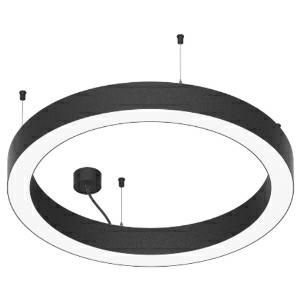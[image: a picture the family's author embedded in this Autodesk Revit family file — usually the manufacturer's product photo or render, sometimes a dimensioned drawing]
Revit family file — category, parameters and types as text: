
# Revit family: glorious_slim_410-9634
name_source: partatom
category: Leuchten
revit_build: Autodesk Revit 2016 (Build: 20190508_0715(x64)
units: mm (PartAtom-declared; Revit-internal decimal feet)

## family parameters
Basisbauteil = Fläche
Beim Laden mit Abzugskörper schneiden = Nein
Bemaßung runder Anschluss = Durchmesser verwenden
Gemeinsam genutzt = Nein
Lichtquelle = Nein
Raumberechnungspunkt = Nein
Teiletyp = Normal

## types (1)
- 410-9634-D01-H27 (1 x LED, 405.68 lm, 3.1 W, 2700K)
    Beschreibung = GLORIOUS SLIM
    CIE Flux Codes = 48 79 96 100 78
    Color Rendering = 1A/90…99
    Color Temperature = 2700K
    Height = 90 mm
    Hersteller = Prolicht
    Lamp Light Flux = 405.68 lm
    Lamp Power = 3.1 W
    Lamp count = 1
    Lampe = 1 x LED
    Length = 144 mm
    Luminous efficacy = 103 lm/W
    ModVariant = Nein
    Modell = 410-9634
    Mounting Place = Ceiling
    Mounting Type = Pendant
    Number of Poles = 1
    OnlyDefault = Ja
    Power Factor = 1
    Product Name = GLORIOUS SLIM
    Product group = Suspended lights
    ProductGroupID = 941
    Protection Class = Protection class
    Protection Degree = Degree of protection
    RLX_Detail_Level = 1
    RlxData = <blob elided: 62073 chars, md5=fe7663a7>
    Scheinlast = 50 VA
    Socket = socket
    Standby Power = 0 W
    System Light Flux = 5089 lm
    System Power = 50 W
    Typenbild = 410-9634.jpg
    Typenkommentare = DIFFUSER Opal (01),LED COLOUR DIR 2700 K (27)
    URL = http://relux.com
    VarID = 410-9634-d01-h27
    Voltage = 0 V
    Vorgabe-Ansicht = 1800 mm
    Weight = 0.00 kg
    Width = 65 mm

## geometry (parser evidence)
native form markers: Blend x4, Sweep x46
no freeform markers — native parametric forms only
